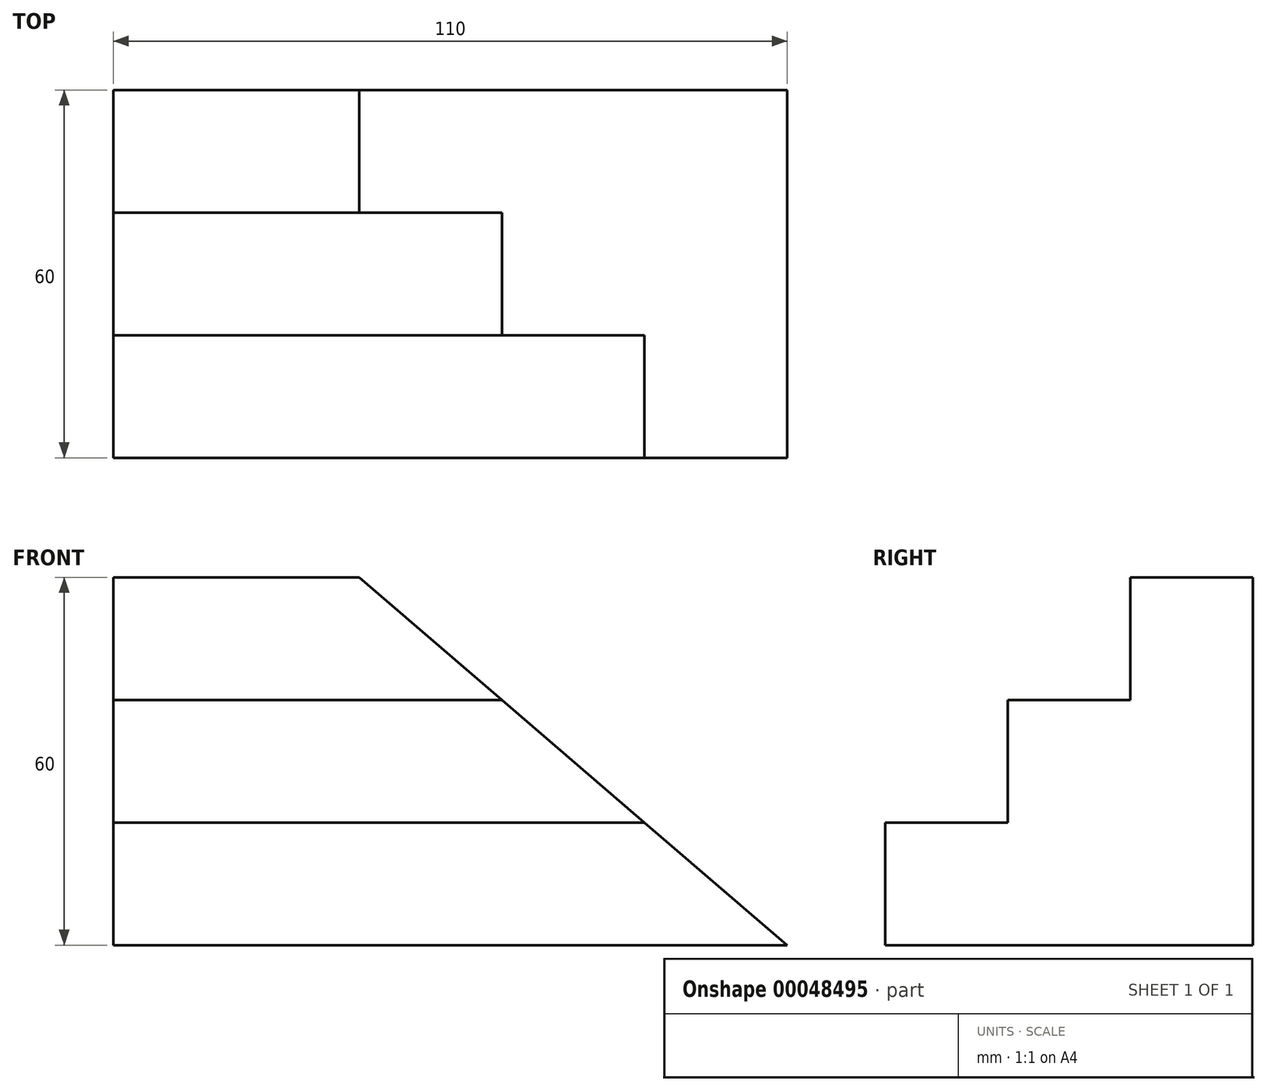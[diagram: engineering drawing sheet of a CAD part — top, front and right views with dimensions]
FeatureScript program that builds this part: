
annotation { "Feature Type Name" : "Feature", "Feature Type Description" : "" }
export const myFeature = defineFeature(function(context is Context, id is Id, definition is map)
    precondition{}
    {
        {
            var Q0;
            Q0=qCreatedBy(makeId("Right.planeOp"),FACE);
            var sketch = newSketch(context, id + "F0", { "sketchPlane" : qUnion([Q0])});
            skLineSegment(sketch, "E0", {"start": v(0, 0) * mm, "end": v(60, 0) * mm});
            skLineSegment(sketch, "E1", {"start": v(60, 0) * mm, "end": v(60, 60) * mm});
            skLineSegment(sketch, "E2", {"start": v(60, 60) * mm, "end": v(40, 60) * mm});
            skLineSegment(sketch, "E3", {"start": v(40, 60) * mm, "end": v(40, 40) * mm});
            skLineSegment(sketch, "E4", {"start": v(40, 40) * mm, "end": v(20, 40) * mm});
            skLineSegment(sketch, "E5", {"start": v(20, 40) * mm, "end": v(20, 20) * mm});
            skLineSegment(sketch, "E6", {"start": v(20, 20) * mm, "end": v(0, 20) * mm});
            skLineSegment(sketch, "E7", {"start": v(0, 20) * mm, "end": v(0, 0) * mm});
            skSolve(sketch);
        }
        {
            var Q0;
            Q0=makeQuery(id+"F0.imprint","IMPRINT",FACE,{"disambiguationData":[TD([[makeQuery(id+"F0.imprint","IMPRINT",EDGE,{"derivedFrom":sQuery(id+"F0.wireOp",EDGE,"E0")}),1.0]])]});
            extrude(context, id + "F1", {"entities" : qUnion([Q0]), "depth" : 110 * mm});
        }
        {
            var Q0;
            Q0=makeQuery(id+"F1.opExtrude","SWEPT_FACE",FACE,{"disambiguationData":[OSD([sQuery(id+"F0.wireOp",EDGE,"E2")])]});
            var sketch = newSketch(context, id + "F2", { "sketchPlane" : qUnion([Q0])});
            skLineSegment(sketch, "E8", {"start": v(40, 60) * mm, "end": v(40, 40) * mm});
            skSolve(sketch);
        }
        {
            var Q0;
            Q0=makeQuery(id+"F1.opExtrude","SWEPT_FACE",FACE,{"disambiguationData":[OSD([sQuery(id+"F0.wireOp",EDGE,"E1")])]});
            var sketch = newSketch(context, id + "F3", { "sketchPlane" : qUnion([Q0])});
            skLineSegment(sketch, "E9", {"start": v(-40.15, 60) * mm, "end": v(-110, 0) * mm});
            skSolve(sketch);
        }
        {
            var Q0;
            {var subQ2=sQuery(id+"F3.wireOp",EDGE,"E9");Q0=makeQuery(id+"F3.imprint","IMPRINT",FACE,{"disambiguationData":[TD([[makeQuery(id+"F3.imprint","IMPRINT",EDGE,{"derivedFrom":subQ2}),-1.0]])]});}
            extrude(context, id + "F4", {"entities" : qUnion([Q0]), "operationType" : NewBodyOperationType.REMOVE, "endBound" : BoundingType.THROUGH_ALL, "oppositeDirection" : true, "depth" : 25 * mm});
        }
    });
